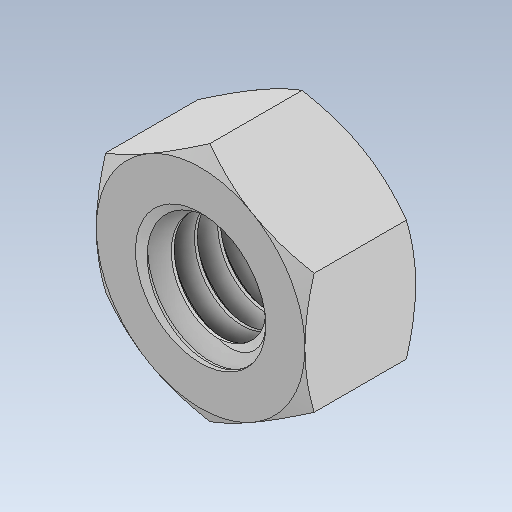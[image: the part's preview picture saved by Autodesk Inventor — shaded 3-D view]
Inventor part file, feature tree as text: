
AUTODESK INVENTOR PART (.ipt)
format: ipt  version: 2023 (Build 270158000, 158)  size: 300,544 bytes
history: native  units: in
note: dims shown in document units (in); Inventor stores cm internally (conversion verified against a paired STEP export)
features: mirror x1
ambient origin geometry x8: Origin, YZ Plane, XZ Plane, XY Plane, X Axis, Y Axis, Z Axis, Center Point
bodies: Solid1 (feature_tree)
feature tree (1):
  mirror  "Mirror1"
